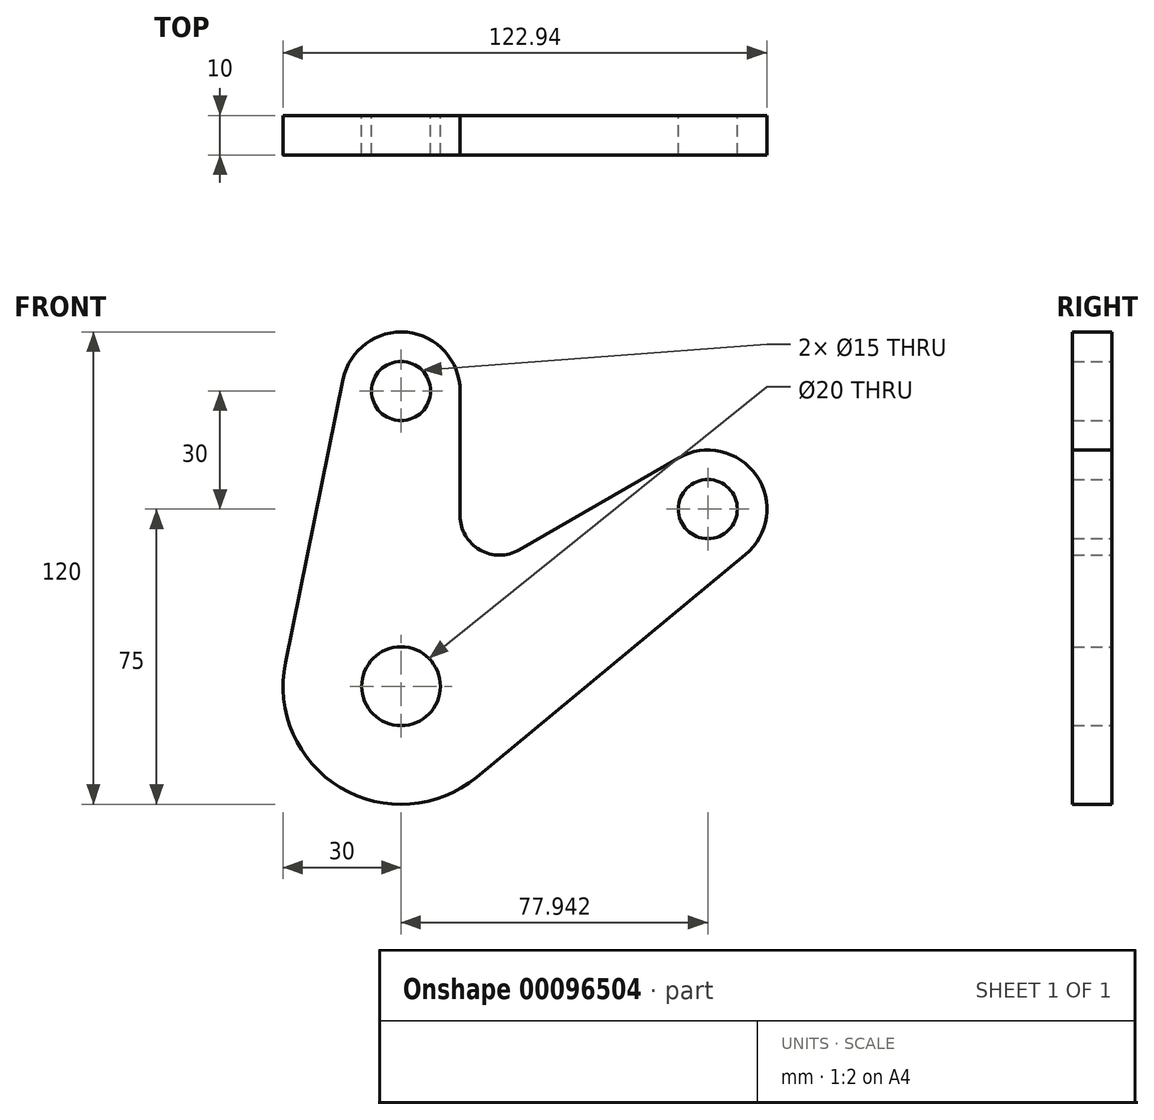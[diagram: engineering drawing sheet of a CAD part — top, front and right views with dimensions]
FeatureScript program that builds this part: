
annotation { "Feature Type Name" : "Feature", "Feature Type Description" : "" }
export const myFeature = defineFeature(function(context is Context, id is Id, definition is map)
    precondition{}
    {
        {
            var Q0;
            Q0=qCreatedBy(makeId("Front.planeOp"),FACE);
            var sketch = newSketch(context, id + "F0", { "sketchPlane" : qUnion([Q0])});
            skCircle(sketch, "E0", {"center": v(0, 0) * mm, "radius": 10 * mm});
            skArc(sketch, "E1", {"start": v(-29.4, 6) * mm, "mid": v(-15.44, -25.72) * mm, "end": v(19.12, -23.12) * mm});
            skArc(sketch, "E2", {"start": v(15, 75) * mm, "mid": v(1.5, 89.92) * mm, "end": v(-14.7, 78) * mm});
            skArc(sketch, "E3", {"start": v(87.5, 33.44) * mm, "mid": v(90.26, 53.56) * mm, "end": v(70.44, 58) * mm});
            skLineSegment(sketch, "E4", {"start": v(-14.7, 78) * mm, "end": v(-29.4, 6) * mm});
            skLineSegment(sketch, "E5", {"start": v(30, 34.64) * mm, "end": v(70.44, 58) * mm});
            skLineSegment(sketch, "E6", {"start": v(87.5, 33.44) * mm, "end": v(19.12, -23.12) * mm});
            skArc(sketch, "E7", {"start": v(15, 43.3) * mm, "mid": v(20, 34.64) * mm, "end": v(30, 34.64) * mm});
            skLineSegment(sketch, "E8", {"start": v(15, 75) * mm, "end": v(15, 43.3) * mm});
            skCircle(sketch, "E9", {"center": v(0, 75) * mm, "radius": 7.5 * mm});
            skCircle(sketch, "E10", {"center": v(77.94, 45) * mm, "radius": 7.5 * mm});
            skLineSegment(sketch, "E11", {"start": v(0, 75) * mm, "end": v(0, 0) * mm, "construction": true});
            skLineSegment(sketch, "E12", {"start": v(77.94, 45) * mm, "end": v(0, 0) * mm, "construction": true});
            skSolve(sketch);
        }
        {
            var Q0;
            Q0 = qSketchRegion(id + "F0", true);
            extrude(context, id + "F1", {"entities" : qUnion([Q0]), "depth" : 10 * mm});
        }
    });
